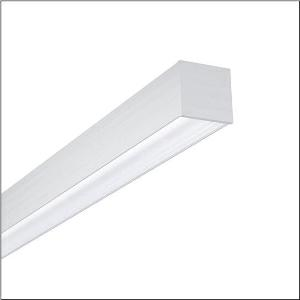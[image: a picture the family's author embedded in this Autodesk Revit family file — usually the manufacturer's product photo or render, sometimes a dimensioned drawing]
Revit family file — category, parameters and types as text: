
# Revit family: silica_r_5mx21bd1e4a_4ae4
name_source: partatom
category: Lighting Fixtures
units: mm (PartAtom-declared; Revit-internal decimal feet)

## family parameters
Cut with Voids When Loaded = No
Host = Face
Light Source = No
Part Type = Normal
Room Calculation Point = No
Round Connector Dimension = Use Diameter
Shared = No

## types (1)
- --- (1 x LED, 4950 lm, 29.3 W, 4000K)
    Apparent Load = 29 VA
    CIE Flux Codes = 82 97 100 100 100
    Color Rendering = 80
    Color Temperature = 4000K
    Default Elevation = 1800 mm
    Description = Silica®, office luminaire, of aluminium, light emission: direct distribution, primary light characteristic: symmetric, installation type: surface-mounted, LED, rated luminous flux: 4.950lm, luminous efficacy: 169lm/W, light colour: 840, colour temperature: 4000K, control gear: ECG DALI, with terminal, 3+2-pole, max. 2.5mm², mains connection: 230V, AC, 50/60Hz, rated input power: 29W, luminaire housing, of aluminium, anodised, silver, length: 1.442mm, width: 65mm, height: 64mm, protection rating (complete): IP20, insulation class (complete): insulation class I (protective earthing), certification: CE, permissible operating ambient temperature: 0..+35°C, standard: EN 50419, packaging unit: 1 piece
    Height = 64 mm
    Lamp = 1 x LED
    Lamp Light Flux = 4950 lm
    Lamp Power = 29.3 W
    Lamp count = 1
    Length = 1442 mm
    Luminous efficacy = 169 lm/W
    Manufacturer = Siteco
    ModVariant = No
    Model = 5MX21BD1E4A
    Mounting Place = Ceiling
    Mounting Type = Surface mounted
    Number of Poles = 1
    OnlyDefault = Yes
    Power Factor = 1
    Product Name = Silica®
    Product group = office luminaire | ceiling mounted
    ProductGroupID = 304
    Protection Class = Protection class I
    Protection Degree = IP 20
    RLX_Detail_Level = 1
    RLX_Emergency_Light_Flux = 0 lm
    RLX_Emergency_Type = 0
    RLX_Emergency_Type_DB = No
    RlxData = <blob elided: 27253 chars, md5=92c3ce4a>
    Socket = socket
    Standby Power = 0 W
    System Light Flux = 4950 lm
    System Power = 29 W
    Type Comments = factory setting: luminous flux: 100 % | dim-lin: 254 | 163 mA
    Type Image = l_1004827.jpg
    URL = http://relux.com
    VarID = @adj_173222
    Voltage = 0 V
    Weight = 0.00 kg
    Width = 66 mm

## geometry (parser evidence)
native form markers: Blend x4, Sweep x10
no freeform markers — native parametric forms only
